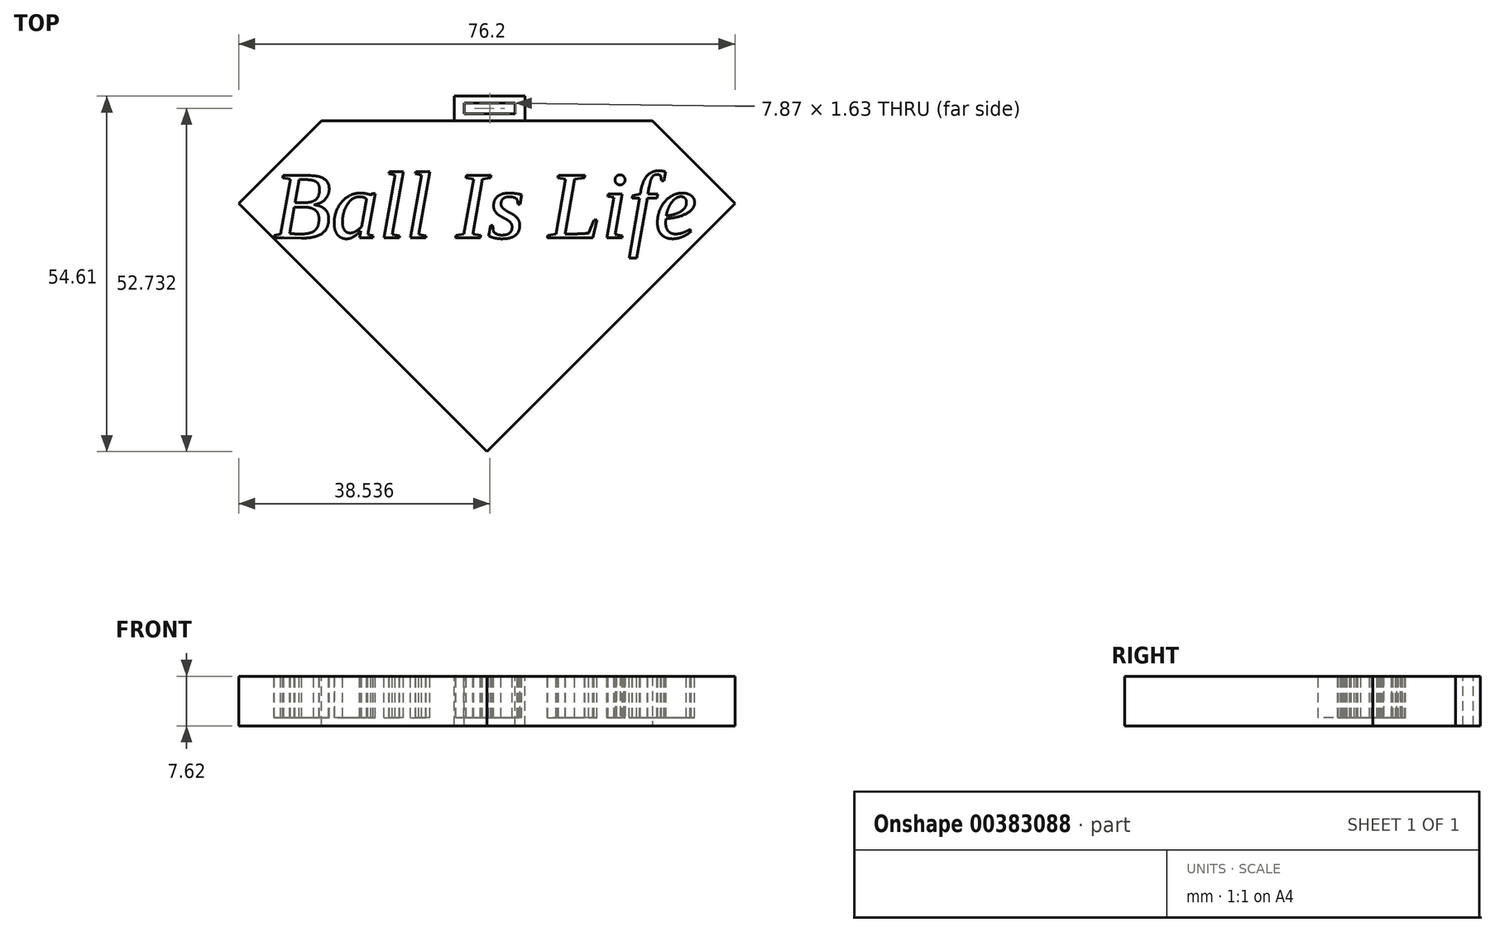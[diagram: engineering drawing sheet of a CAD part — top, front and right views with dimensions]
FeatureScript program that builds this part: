
annotation { "Feature Type Name" : "Feature", "Feature Type Description" : "" }
export const myFeature = defineFeature(function(context is Context, id is Id, definition is map)
    precondition{}
    {
        {
            var Q0;
            Q0=qCreatedBy(makeId("Top.planeOp"),FACE);
            var sketch = newSketch(context, id + "F0", { "sketchPlane" : qUnion([Q0])});
            skLineSegment(sketch, "E0.bottom", {"start": v(-35.94, 39.13) * mm, "end": v(40.26, 39.13) * mm});
            skLineSegment(sketch, "E0.top", {"start": v(-35.94, -11.67) * mm, "end": v(40.26, -11.67) * mm});
            skLineSegment(sketch, "E0.left", {"start": v(-35.94, 39.13) * mm, "end": v(-35.94, -11.67) * mm});
            skLineSegment(sketch, "E0.right", {"start": v(40.26, 39.13) * mm, "end": v(40.26, -11.67) * mm});
            skSolve(sketch);
        }
        {
            var Q0;
            Q0=makeQuery(id+"F0.imprint","IMPRINT",FACE,{"disambiguationData":[TD([[makeQuery(id+"F0.imprint","IMPRINT",EDGE,{"derivedFrom":sQuery(id+"F0.wireOp",EDGE,"E0.bottom")}),-1.0]])]});
            extrude(context, id + "F1", {"entities" : qUnion([Q0]), "depth" : 7.62 * mm});
        }
        {
            var Q0;
            Q0=makeQuery(id+"F1.opExtrude","SWEPT_EDGE",EDGE,{"disambiguationData":[OSD([sQuery(id+"F0.wireOp",EDGE,"E0.bottom"),sQuery(id+"F0.wireOp",EDGE,"E0.left")])]});
            chamfer(context, id + "F2", {"entities" : qUnion([Q0]), "width" : 12.7 * mm, "tangentPropagation" : true});
        }
        {
            var Q0;
            Q0=makeQuery(id+"F1.opExtrude","SWEPT_EDGE",EDGE,{"disambiguationData":[OSD([sQuery(id+"F0.wireOp",EDGE,"E0.bottom"),sQuery(id+"F0.wireOp",EDGE,"E0.right")])]});
            chamfer(context, id + "F3", {"entities" : qUnion([Q0]), "width" : 12.7 * mm, "tangentPropagation" : true});
        }
        {
            var Q0;
            Q0=makeQuery(id+"F1.opExtrude","SWEPT_EDGE",EDGE,{"disambiguationData":[OSD([sQuery(id+"F0.wireOp",EDGE,"E0.top"),sQuery(id+"F0.wireOp",EDGE,"E0.right")])]});
            chamfer(context, id + "F4", {"entities" : qUnion([Q0]), "width" : 38.1 * mm, "tangentPropagation" : true});
        }
        {
            var Q0;
            Q0=makeQuery(id+"F1.opExtrude","SWEPT_EDGE",EDGE,{"disambiguationData":[OSD([sQuery(id+"F0.wireOp",EDGE,"E0.top"),sQuery(id+"F0.wireOp",EDGE,"E0.left")])]});
            chamfer(context, id + "F5", {"entities" : qUnion([Q0]), "width" : 38.1 * mm, "tangentPropagation" : true});
        }
        {
            var Q0;
            Q0=makeQuery(id+"F1.opExtrude","CAP_FACE",FACE,{"disambiguationData":[OSD([sQuery(id+"F0.wireOp",EDGE,"E0.bottom"),sQuery(id+"F0.wireOp",EDGE,"E0.top"),sQuery(id+"F0.wireOp",EDGE,"E0.left"),sQuery(id+"F0.wireOp",EDGE,"E0.right")])],"isStart":false});
            var sketch = newSketch(context, id + "F6", { "sketchPlane" : qUnion([Q0])});
            skText(sketch, "E1", { "text": "Ball Is Life", "fontName": "Tinos-Italic.ttf"});
            const initialGuessF6  = {"E1": [-0.03066, 0.02116, 1, 0, 0.01054]};
            skSetInitialGuess(sketch, initialGuessF6);
            skSolve(sketch);
        }
        {
            var Q0;
            Q0 = qSketchRegion(id + "F6", true);
            extrude(context, id + "F7", {"entities" : qUnion([Q0]), "operationType" : NewBodyOperationType.REMOVE, "oppositeDirection" : true, "depth" : 6.35 * mm});
        }
        {
            var Q0;
            Q0=makeQuery(id+"F1.opExtrude","SWEPT_FACE",FACE,{"disambiguationData":[OSD([sQuery(id+"F0.wireOp",EDGE,"E0.bottom")])]});
            var sketch = newSketch(context, id + "F8", { "sketchPlane" : qUnion([Q0])});
            skLineSegment(sketch, "E2.bottom", {"start": v(2.83, 0) * mm, "end": v(-8.02, 0) * mm});
            skLineSegment(sketch, "E2.top", {"start": v(2.83, 7.59) * mm, "end": v(-8.02, 7.59) * mm});
            skLineSegment(sketch, "E2.left", {"start": v(2.83, 0) * mm, "end": v(2.83, 7.59) * mm});
            skLineSegment(sketch, "E2.right", {"start": v(-8.02, 0) * mm, "end": v(-8.02, 7.59) * mm});
            skPoint(sketch, "E2.middle", {"position": v(-2.6, 3.8) * mm});
            skSolve(sketch);
        }
        {
            var Q0;
            Q0 = qSketchRegion(id + "F8", true);
            extrude(context, id + "F9", {"entities" : qUnion([Q0]), "operationType" : NewBodyOperationType.ADD, "depth" : 3.8 * mm});
        }
        {
            var Q0;
            Q0=makeQuery(id+"F9.opExtrude","SWEPT_FACE",FACE,{"disambiguationData":[OSD([sQuery(id+"F8.wireOp",EDGE,"E2.top")])]});
            var sketch = newSketch(context, id + "F10", { "sketchPlane" : qUnion([Q0])});
            skLineSegment(sketch, "E3.bottom", {"start": v(6.53, 40.25) * mm, "end": v(-1.34, 40.25) * mm});
            skLineSegment(sketch, "E3.top", {"start": v(6.53, 41.88) * mm, "end": v(-1.34, 41.88) * mm});
            skLineSegment(sketch, "E3.left", {"start": v(6.53, 40.25) * mm, "end": v(6.53, 41.88) * mm});
            skLineSegment(sketch, "E3.right", {"start": v(-1.34, 40.25) * mm, "end": v(-1.34, 41.88) * mm});
            skPoint(sketch, "E3.middle", {"position": v(2.6, 41.06) * mm});
            skPoint(sketch, "E3.middle.positionSnap0", {"position": v(2.6, 39.13) * mm});
            skPoint(sketch, "E3.centerSnap0", {"position": v(2.6, 39.13) * mm});
            skSolve(sketch);
        }
        {
            var Q0;
            Q0 = qSketchRegion(id + "F10", true);
            extrude(context, id + "F11", {"entities" : qUnion([Q0]), "operationType" : NewBodyOperationType.REMOVE, "oppositeDirection" : true, "depth" : 25.4 * mm});
        }
    });
